# Revit family: oventrop_hydrocontrol-vtr_1060103-16rfa
name_source: partatom
category: Арматура трубопроводов
revit_build: Autodesk Revit 2017 (Build: 20160225_1515(x64)
units: mm (PartAtom-declared; Revit-internal decimal feet)

## family parameters
Всегда вертикально = Да
Заголовок OmniClass = Adjusting/Controlling Valves for Liquid Services
На основе рабочей плоскости = Нет
Номер OmniClass = 23.65.55.14.17
Общий = Нет
При загрузке вырезать с полостями = Нет
Размер круглого соединителя = Использовать радиус
Тип детали = Клапан - Вставляется

## types (7) — shared parameters
Angle = 50.00°
Article Description = Bronze double regulating and commissioning valves
Article Type = Hydrocontrol VTR 10601
Black = Color RGB 35-35-35
Bronze = Color RGB 156-122-90
Custom = Нет
EMCS Version = 2.0
ETIM Article Class = EC011463
Family Version = 10.14
Hb4 = 18 мм
Hb5 = 3 мм
Hlp1 = 22 мм
IFCExportAs = IfcValveType
IFCExportType = PRESSUREREDUCING
Lgt2 = 11 мм
Manufacturer URL = http://www.oventrop.de
Pressure Drop = 0.0 Па
Product Line = Oventrop
Revit Version = 2015
r1 = 2 мм
r2 = 3 мм
Группа модели = Hydrocontrol VTR 10601
Изготовитель = Oventrop
Описание = Bronze double regulating and commissioning valves

## per-type parameters (varying)
| type | GTIN | Hb1 | Hb3 | Hb8 | Height | L2 | Length | Lgt1 | Manufacturer Art. No. | Measure_port | NominalDiameter | NutDimension | OuterDiameter | Rad1 | Rad2 | Rad3 | Rad4 | Rad5 | SW2 | Threaded_Lenght | URL | e2 | e3 |
| DN 40 | 4026755124989 | 154 мм | 5 мм | 50 мм | 138 мм | 9.466 мм | 120 мм | 21.1 мм | 1060112 | 8 мм | 38.100 мм | 55 мм | 48.3 мм | 22.3 мм | 20.3 мм | 22.8 мм | 25.3 мм | 27.3 мм | 63.509 мм | 19.1 мм | www.stabiplan.com | 4.5 мм | 2.344 мм |
| DN 50 | 4026755124996 | 167 мм | 15 мм | 60 мм | 148 мм | 13.15 мм | 150 мм | 27.7 мм | 1060116 | 10 мм | 50.800 мм | 70 мм | 60.3 мм | 30.2 мм | 28.2 мм | 30.7 мм | 33.2 мм | 35.2 мм | 80.829 мм | 25.7 мм | www.stabiplan.com | 4.5 мм | 2.656 мм |
| DN 32 | 4026755124972 | 151 мм | 1 мм | 50 мм | 136 мм | 7.927 мм | 110 мм | 21.1 мм | 1060110 | 7 мм | 31.750 мм | 50 мм | 42.4 мм | 19 мм | 17 мм | 19.5 мм | 22 мм | 24 мм | 57.735 мм | 19.1 мм | www.stabiplan.com | 4.5 мм | 2 мм |
| DN 25 | 4026755124965 | 129 мм | 13 мм | 45 мм | 119 мм | 6.482 мм | 97.5 мм | 18.8 мм | 1060108 | 6 мм | 25.400 мм | 41 мм | 33.7 мм | 15.9 мм | 13.9 мм | 16.4 мм | 18.9 мм | 20.9 мм | 47.343 мм | 16.8 мм | www.stabiplan.com | 3.5 мм | 1.688 мм |
| DN 20 | 4026755124958 | 125 мм | 11 мм | 35 мм | 116 мм | 4.989 мм | 84 мм | 16.5 мм | 1060106 | 5 мм | 19.050 мм | 32 мм | 26.9 мм | 12.7 мм | 10.7 мм | 13.2 мм | 15.7 мм | 17.7 мм | 36.95 мм | 14.5 мм | www.stabiplan.com | 3.5 мм | 1.5 мм |
| DN 15 | 4026755124941 | 122 мм | 15 мм | 35 мм | 114 мм | 3.497 мм | 80 мм | 15.2 мм | 1060104 | 5 мм | 12.700 мм | 27 мм | 21.3 мм | 9.5 мм | 7.5 мм | 10 мм | 12.5 мм | 14.5 мм | 31.177 мм | 13.2 мм | www.stabiplan.com | 2.5 мм | 1.25 мм |
| DN 10 | 4026755124934 | 122 мм | 15 мм | 35 мм | 114 мм | 3.497 мм | 73 мм | 12.1 мм | 1060103 | 5 мм | 9.525 мм | 27 мм | 17.2 мм | 9.5 мм | 7.5 мм | 10 мм | 12.5 мм | 14.5 мм | 31.177 мм | 10.1 мм | http://file-system.ru | 2.5 мм | 1.125 мм |

## geometry (parser evidence)
native form markers: Sweep x2
no freeform markers — native parametric forms only
